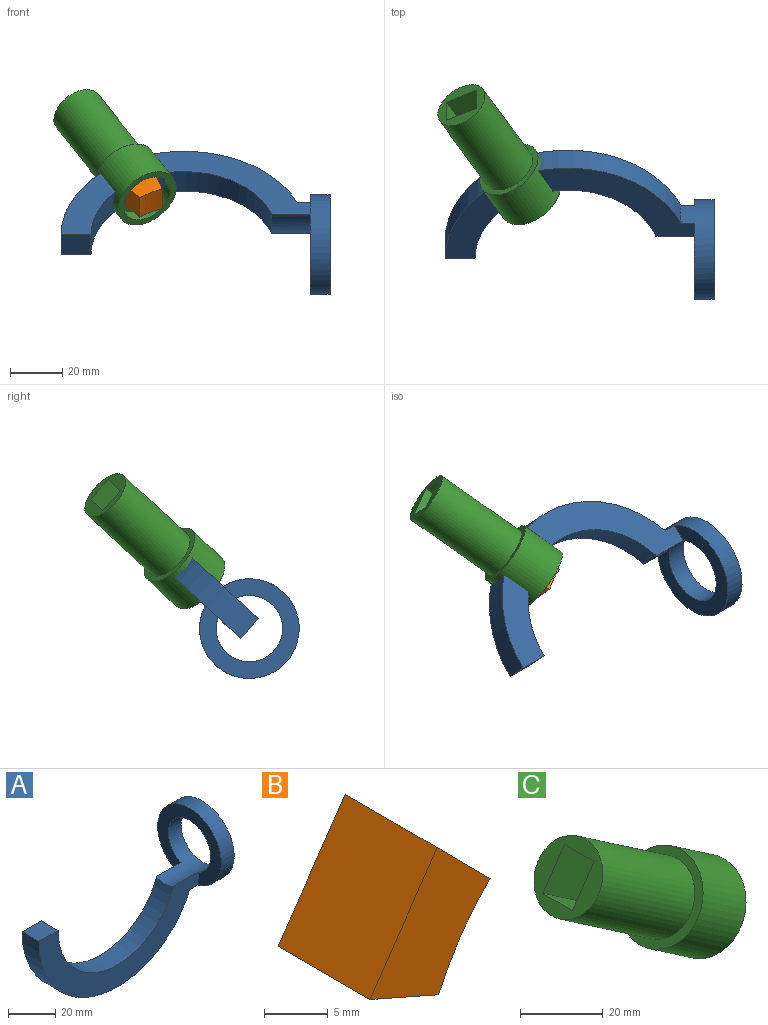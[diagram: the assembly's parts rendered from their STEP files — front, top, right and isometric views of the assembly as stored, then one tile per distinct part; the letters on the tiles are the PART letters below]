
ASSEMBLY  parts=3 mates=1
PART A: 9 faces, bbox 102.9x38.1x66.1 mm
  f0: cylinder r=35.61mm len=69.26mm, axis (0,1,0), area 1008.3mm2, adj f1,f2,f4,f5
  f1: plane 95.28x47.02mm, normal (0,-1,0), area 1371.7mm2, adj f0,f3,f4,f5,f6,f8
  f2: plane 95.28x47.02mm, normal (0,1,0), area 1371.7mm2, adj f0,f3,f4,f5,f6,f8
  f3: cylinder r=47.02mm len=90.31mm, axis (0,1,0), area 1304mm2, adj f1,f2,f4,f6
  f4: plane 11.41x10.16mm, normal (0,0,1), area 116mm2, adj f0,f1,f2,f3
  f5: cylinder r=12.7mm len=25.4mm, axis (-1,0,0), area 763.4mm2, adj f0,f1,f2,f7,f8
  f6: cylinder r=19.05mm len=38.1mm, axis (-1,0,0), area 965.3mm2, adj f1,f2,f3,f7,f8
  f7: plane 38.1x38.1mm, normal (1,0,0), area 633.4mm2, adj f5,f6
  f8: plane 38.1x37.41mm, normal (-1,0,0), area 567.7mm2, adj f1,f2,f5,f6
PART B: 6 faces, bbox 13.3x10.2x14.2 mm
  f0: plane 10.82x10.16mm, normal (-0.82,0,0.57), area 133.3mm2, adj f1,f3,f4,f5
  f1: plane 10.16x7.58mm, normal (-0.4,0,-0.92), area 84.1mm2, adj f0,f2,f4,f5
  f2: cylinder r=27.01mm len=10.16mm, axis (0,1,0), area 102.7mm2, adj f1,f3,f4,f5
  f3: plane 10.16x5.87mm, normal (0.71,0,0.7), area 84.1mm2, adj f0,f2,f4,f5
  f4: plane 14.16x13.26mm, normal (0,-1,0), area 91.1mm2, adj f0,f1,f2,f3
  f5: plane 14.16x13.26mm, normal (0,1,0), area 91.1mm2, adj f0,f1,f2,f3
PART C: 11 faces, bbox 59.1x25.4x50.5 mm
  f0: cylinder r=10.25mm len=20.5mm, axis (0.82,0,-0.57), area 327.1mm2, adj f3,f10
  f1: cylinder r=12.7mm len=31mm, axis (0.82,0,-0.57), area 1418.8mm2, adj f2,f3
  f2: plane 25.4x20.94mm, normal (-0.82,0,0.57), area 176.8mm2, adj f1,f4
  f3: plane 25.4x20.94mm, normal (0.82,0,-0.57), area 176.8mm2, adj f0,f1
  f4: cylinder r=10.25mm len=43.01mm, axis (0.82,0,-0.57), area 2453.3mm2, adj f2,f9
  f5: plane 41.89x28.74mm, normal (0.57,0,0.82), area 516.1mm2, adj f6,f8,f9,f10
  f6: plane 49.31x39.56mm, normal (0,-1,0), area 666.7mm2, adj f5,f7,f9,f10
  f7: plane 41.89x28.74mm, normal (-0.57,0,-0.82), area 516.1mm2, adj f6,f8,f9,f10
  f8: plane 49.31x39.56mm, normal (0,1,0), area 666.7mm2, adj f5,f7,f9,f10
  f9: plane 20.5x16.9mm, normal (-0.82,0,0.57), area 196.6mm2, adj f4,f5,f6,f7,f8
  f10: plane 20.5x16.9mm, normal (0.82,0,-0.57), area 196.6mm2, adj f0,f5,f6,f7,f8
PLACE A rot(axis=(1,0,0),132.8deg) t=(-23.97,-1.26,-0.01)mm
PLACE B rot(axis=(0.64,-0.31,-0.71),148.9deg) t=(-23.97,-1.26,-0.01)mm
PLACE C rot(axis=(0.64,-0.31,-0.71),148.9deg) t=(-23.97,-1.26,-0.01)mm
MATE revolute A.f0 <-> B.f2  axis (0,-0.68,0.73) through (-23.97,-1.26,-0.01)mm
